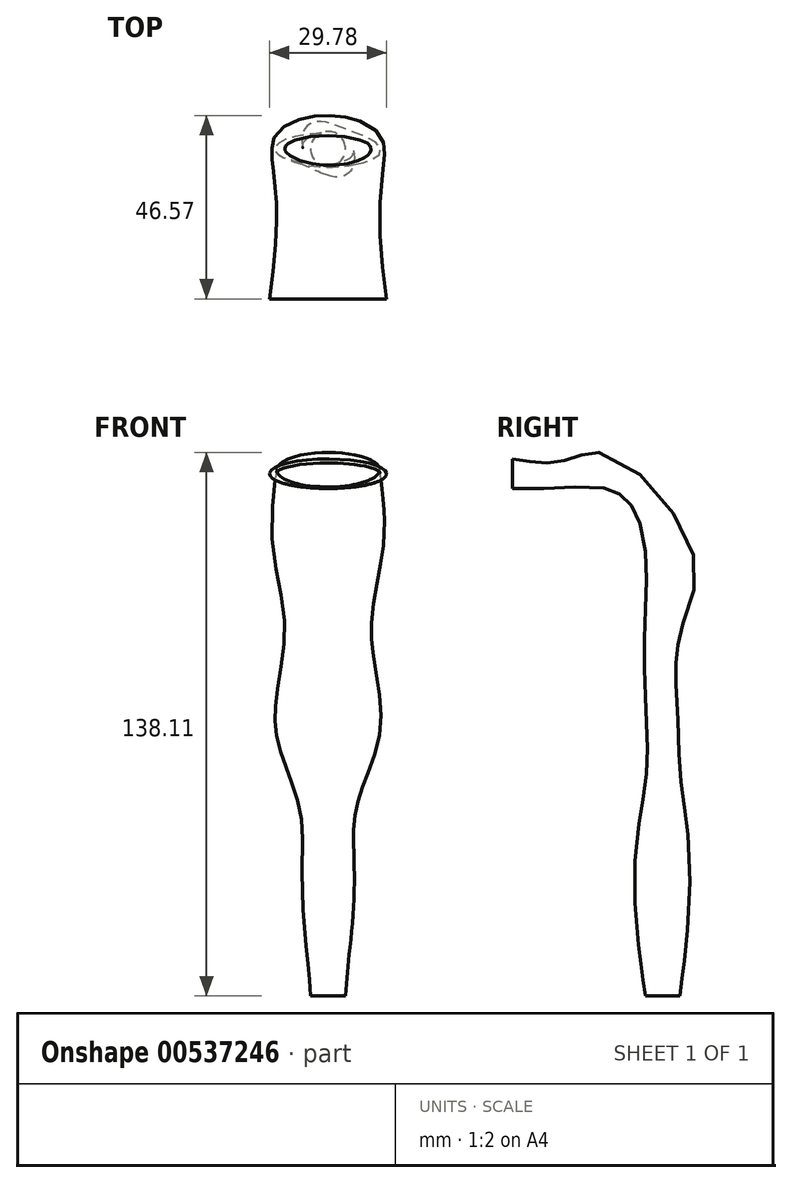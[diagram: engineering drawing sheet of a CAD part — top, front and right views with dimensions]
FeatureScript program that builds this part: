
annotation { "Feature Type Name" : "Feature", "Feature Type Description" : "" }
export const myFeature = defineFeature(function(context is Context, id is Id, definition is map)
    precondition{}
    {
        {
            var Q0;
            Q0=qCreatedBy(makeId("Top.planeOp"),FACE);
            var sketch = newSketch(context, id + "F0", { "sketchPlane" : qUnion([Q0])});
            skEllipse(sketch, "E0", {"center": v(0, 0) * mm, "majorRadius": 13.3 * mm, "minorRadius": 3.99 * mm, "majorAxis": v(1, 0)});
            skSolve(sketch);
        }
        {
            var Q0;
            Q0=qCreatedBy(makeId("Top.planeOp"),FACE);
            cPlane(context, id + "F1", {"entities" : qUnion([Q0]), "cplaneType" : CPlaneType.OFFSET, "offset" : 25.4 * mm, "width" : 152.4 * mm, "height" : 152.4 * mm});
        }
        {
            var Q0;
            Q0=qCreatedBy(id+"F1.planeOp",FACE);
            var sketch = newSketch(context, id + "F2", { "sketchPlane" : qUnion([Q0])});
            skEllipse(sketch, "E1", {"center": v(0, 0) * mm, "majorRadius": 10.98 * mm, "minorRadius": 4.62 * mm, "majorAxis": v(1, 0)});
            skSolve(sketch);
        }
        {
            var Q0;
            Q0=qCreatedBy(id+"F1.planeOp",FACE);
            cPlane(context, id + "F3", {"entities" : qUnion([Q0]), "cplaneType" : CPlaneType.OFFSET, "offset" : 25.4 * mm, "width" : 152.4 * mm, "height" : 152.4 * mm});
        }
        {
            var Q0;
            Q0=qCreatedBy(id+"F3.planeOp",FACE);
            var sketch = newSketch(context, id + "F4", { "sketchPlane" : qUnion([Q0])});
            skEllipse(sketch, "E2", {"center": v(0, 0) * mm, "majorRadius": 14.3 * mm, "minorRadius": 5.31 * mm, "majorAxis": v(1, 0)});
            skSolve(sketch);
        }
        {
            var Q0;
            Q0=qCreatedBy(makeId("Front.planeOp"),FACE);
            cPlane(context, id + "F5", {"entities" : qUnion([Q0]), "cplaneType" : CPlaneType.OFFSET, "offset" : 25.4 * mm, "width" : 152.4 * mm, "height" : 152.4 * mm});
        }
        {
            var Q0;
            Q0=qCreatedBy(id+"F5.planeOp",FACE);
            var sketch = newSketch(context, id + "F6", { "sketchPlane" : qUnion([Q0])});
            skEllipse(sketch, "E3", {"center": v(0, 64.94) * mm, "majorRadius": 13.4 * mm, "minorRadius": 3.4 * mm, "majorAxis": v(1, 0)});
            skSolve(sketch);
        }
        {
            var Q0;
            Q0=qCreatedBy(makeId("Front.planeOp"),FACE);
            cPlane(context, id + "F7", {"entities" : qUnion([Q0]), "cplaneType" : CPlaneType.OFFSET, "offset" : 12.7 * mm, "width" : 152.4 * mm, "height" : 152.4 * mm});
        }
        {
            var Q0;
            Q0=qCreatedBy(id+"F7.planeOp",FACE);
            var sketch = newSketch(context, id + "F8", { "sketchPlane" : qUnion([Q0])});
            skEllipse(sketch, "E4", {"center": v(0, 65.31) * mm, "majorRadius": 13.21 * mm, "minorRadius": 4.44 * mm, "majorAxis": v(1, 0)});
            skSolve(sketch);
        }
        {
            var Q0;
            Q0=qCreatedBy(makeId("Top.planeOp"),FACE);
            cPlane(context, id + "F9", {"entities" : qUnion([Q0]), "cplaneType" : CPlaneType.OFFSET, "offset" : 25.4 * mm, "oppositeDirection" : true, "width" : 152.4 * mm, "height" : 152.4 * mm});
        }
        {
            var Q0;
            Q0=qCreatedBy(id+"F9.planeOp",FACE);
            var sketch = newSketch(context, id + "F10", { "sketchPlane" : qUnion([Q0])});
            skEllipse(sketch, "E5", {"center": v(0, 0) * mm, "majorRadius": 6.51 * mm, "minorRadius": 6.27 * mm, "majorAxis": v(1, 0)});
            skSolve(sketch);
        }
        {
            var Q0;
            Q0=qCreatedBy(id+"F9.planeOp",FACE);
            cPlane(context, id + "F11", {"entities" : qUnion([Q0]), "cplaneType" : CPlaneType.OFFSET, "offset" : 42.16 * mm, "oppositeDirection" : true, "width" : 152.4 * mm, "height" : 152.4 * mm});
        }
        {
            var Q0;
            Q0=qCreatedBy(id+"F11.planeOp",FACE);
            var sketch = newSketch(context, id + "F12", { "sketchPlane" : qUnion([Q0])});
            skCircle(sketch, "E6", {"center": v(0, 0) * mm, "radius": 4.42 * mm});
            skSolve(sketch);
        }
        {
            var Q0;
            Q0=qCreatedBy(id+"F5.planeOp",FACE);
            cPlane(context, id + "F13", {"entities" : qUnion([Q0]), "cplaneType" : CPlaneType.OFFSET, "offset" : 12.7 * mm, "width" : 152.4 * mm, "height" : 152.4 * mm});
        }
        {
            var Q0;
            Q0=qCreatedBy(id+"F13.planeOp",FACE);
            var sketch = newSketch(context, id + "F14", { "sketchPlane" : qUnion([Q0])});
            skEllipse(sketch, "E7", {"center": v(0, 65.12) * mm, "majorRadius": 14.89 * mm, "minorRadius": 3.74 * mm, "majorAxis": v(1, 0)});
            skSolve(sketch);
        }
        {
            var Q0;
            Q0=makeQuery(id+"F12.imprint","IMPRINT",FACE,{"disambiguationData":[TD([[makeQuery(id+"F12.imprint","IMPRINT",EDGE,{"derivedFrom":sQuery(id+"F12.wireOp",EDGE,"E6")}),1.0]])]});
            var Q1;
            Q1=makeQuery(id+"F10.imprint","IMPRINT",FACE,{"disambiguationData":[TD([[makeQuery(id+"F10.imprint","IMPRINT",EDGE,{"derivedFrom":sQuery(id+"F10.wireOp",EDGE,"E5")}),1.0]])]});
            var Q2;
            Q2=makeQuery(id+"F0.imprint","IMPRINT",FACE,{"disambiguationData":[TD([[makeQuery(id+"F0.imprint","IMPRINT",EDGE,{"derivedFrom":sQuery(id+"F0.wireOp",EDGE,"E0")}),1.0]])]});
            var Q3;
            Q3=makeQuery(id+"F2.imprint","IMPRINT",FACE,{"disambiguationData":[TD([[makeQuery(id+"F2.imprint","IMPRINT",EDGE,{"derivedFrom":sQuery(id+"F2.wireOp",EDGE,"E1")}),1.0]])]});
            var Q4;
            Q4=makeQuery(id+"F4.imprint","IMPRINT",FACE,{"disambiguationData":[TD([[makeQuery(id+"F4.imprint","IMPRINT",EDGE,{"derivedFrom":sQuery(id+"F4.wireOp",EDGE,"E2")}),1.0]])]});
            var Q5;
            Q5=makeQuery(id+"F8.imprint","IMPRINT",FACE,{"disambiguationData":[TD([[makeQuery(id+"F8.imprint","IMPRINT",EDGE,{"derivedFrom":sQuery(id+"F8.wireOp",EDGE,"E4")}),1.0]])]});
            var Q6;
            Q6=makeQuery(id+"F6.imprint","IMPRINT",FACE,{"disambiguationData":[TD([[makeQuery(id+"F6.imprint","IMPRINT",EDGE,{"derivedFrom":sQuery(id+"F6.wireOp",EDGE,"E3")}),1.0]])]});
            var Q7;
            Q7=makeQuery(id+"F14.imprint","IMPRINT",FACE,{"disambiguationData":[TD([[makeQuery(id+"F14.imprint","IMPRINT",EDGE,{"derivedFrom":sQuery(id+"F14.wireOp",EDGE,"E7")}),1.0]])]});
            var Q8;
            Q8=sQuery(id+"F12.wireOp",EDGE,"E6");
            var Q9;
            Q9=makeQuery(id+"F10.imprint","IMPRINT",FACE,{"disambiguationData":[TD([[makeQuery(id+"F10.imprint","IMPRINT",EDGE,{"derivedFrom":sQuery(id+"F10.wireOp",EDGE,"E5")}),1.0]])]});
            var Q10;
            Q10=makeQuery(id+"F0.imprint","IMPRINT",FACE,{"disambiguationData":[TD([[makeQuery(id+"F0.imprint","IMPRINT",EDGE,{"derivedFrom":sQuery(id+"F0.wireOp",EDGE,"E0")}),1.0]])]});
            var Q11;
            Q11=makeQuery(id+"F2.imprint","IMPRINT",FACE,{"disambiguationData":[TD([[makeQuery(id+"F2.imprint","IMPRINT",EDGE,{"derivedFrom":sQuery(id+"F2.wireOp",EDGE,"E1")}),1.0]])]});
            var Q12;
            Q12=makeQuery(id+"F4.imprint","IMPRINT",FACE,{"disambiguationData":[TD([[makeQuery(id+"F4.imprint","IMPRINT",EDGE,{"derivedFrom":sQuery(id+"F4.wireOp",EDGE,"E2")}),1.0]])]});
            var Q13;
            Q13=makeQuery(id+"F8.imprint","IMPRINT",FACE,{"disambiguationData":[TD([[makeQuery(id+"F8.imprint","IMPRINT",EDGE,{"derivedFrom":sQuery(id+"F8.wireOp",EDGE,"E4")}),1.0]])]});
            var Q14;
            Q14=sQuery(id+"F6.wireOp",EDGE,"E3");
            var Q15;
            Q15=makeQuery(id+"F14.imprint","IMPRINT",FACE,{"disambiguationData":[TD([[makeQuery(id+"F14.imprint","IMPRINT",EDGE,{"derivedFrom":sQuery(id+"F14.wireOp",EDGE,"E7")}),1.0]])]});
            loft(context, id + "F15", {"bodyType" : ToolBodyType.SURFACE, "sheetProfilesArray" : [{ "sheetProfileEntities" : qUnion([Q0]) }, { "sheetProfileEntities" : qUnion([Q1]) }, { "sheetProfileEntities" : qUnion([Q2]) }, { "sheetProfileEntities" : qUnion([Q3]) }, { "sheetProfileEntities" : qUnion([Q4]) }, { "sheetProfileEntities" : qUnion([Q5]) }, { "sheetProfileEntities" : qUnion([Q6]) }, { "sheetProfileEntities" : qUnion([Q7]) }], "wireProfilesArray" : [{ "wireProfileEntities" : qUnion([Q8]) }, { "wireProfileEntities" : qUnion([Q9]) }, { "wireProfileEntities" : qUnion([Q10]) }, { "wireProfileEntities" : qUnion([Q11]) }, { "wireProfileEntities" : qUnion([Q12]) }, { "wireProfileEntities" : qUnion([Q13]) }, { "wireProfileEntities" : qUnion([Q14]) }, { "wireProfileEntities" : qUnion([Q15]) }]});
        }
    });
